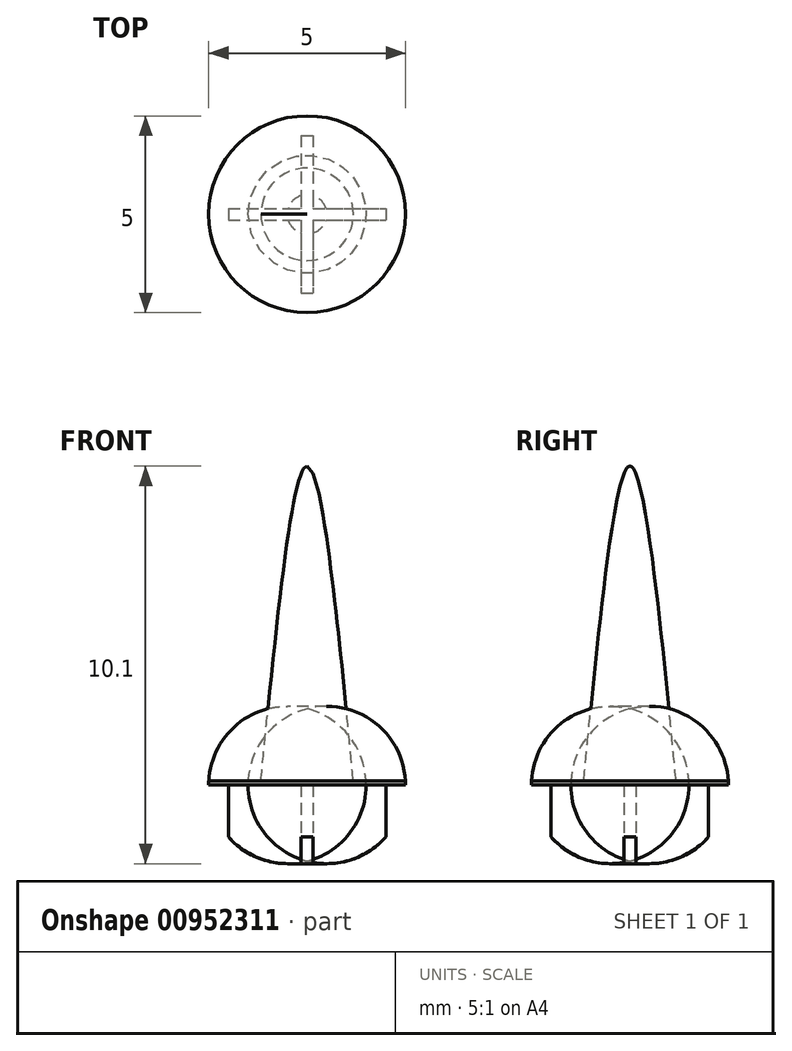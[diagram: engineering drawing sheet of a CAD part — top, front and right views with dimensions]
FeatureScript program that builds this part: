
annotation { "Feature Type Name" : "Feature", "Feature Type Description" : "" }
export const myFeature = defineFeature(function(context is Context, id is Id, definition is map)
    precondition{}
    {
        {
            var Q0;
            Q0=qCreatedBy(makeId("Top.planeOp"),FACE);
            var sketch = newSketch(context, id + "F0", { "sketchPlane" : qUnion([Q0])});
            skCircle(sketch, "E0", {"center": v(0, 0) * mm, "radius": 2.5 * mm});
            skSolve(sketch);
        }
        {
            var Q0;
            Q0=qSketchRegion(id+"F0",true);
            extrude(context, id + "F1", {"entities" : qUnion([Q0]), "depth" : 2.1 * mm, "offsetDistance" : 25 * mm});
        }
        {
            var Q0;
            Q0=makeQuery(id+"F1.opExtrude","CAP_FACE",FACE,{"disambiguationData":[OSD([sQuery(id+"F0.wireOp",EDGE,"E0")])],"isStart":false});
            var sketch = newSketch(context, id + "F2", { "sketchPlane" : qUnion([Q0])});
            skCircle(sketch, "E1", {"center": v(0, 0) * mm, "radius": 1.18 * mm});
            skSolve(sketch);
        }
        {
            var Q0;
            Q0=makeQuery(id+"F2.imprint","IMPRINT",FACE,{"disambiguationData":[TD([[makeQuery(id+"F2.imprint","IMPRINT",EDGE,{"derivedFrom":sQuery(id+"F2.wireOp",EDGE,"E1")}),-1.0]])]});
            cPlane(context, id + "F3", {"entities" : qUnion([Q0]), "cplaneType" : CPlaneType.OFFSET, "offset" : 8 * mm, "width" : 150 * mm, "height" : 150 * mm});
        }
        {
            var Q0;
            Q0=qCreatedBy(id+"F3.planeOp",FACE);
            var sketch = newSketch(context, id + "F4", { "sketchPlane" : qUnion([Q0])});
            skCircle(sketch, "E2", {"center": v(0, 0) * mm, "radius": 0.1 * mm});
            skSolve(sketch);
        }
        {
            var Q0;
            Q0=makeQuery(id+"F2.imprint","IMPRINT",FACE,{"disambiguationData":[TD([[makeQuery(id+"F2.imprint","IMPRINT",EDGE,{"derivedFrom":sQuery(id+"F2.wireOp",EDGE,"E1")}),1.0]])]});
            var Q1;
            Q1=sQuery(id+"F4.wireOp",VERTEX,"E2.center");
            loft(context, id + "F5", {"operationType" : NewBodyOperationType.ADD, "sheetProfilesArray" : [{ "sheetProfileEntities" : qUnion([Q0]) }, { "sheetProfileEntities" : qUnion([Q1]) }], "endCondition" : LoftEndDerivativeType.TANGENT_TO_PROFILE, "endMagnitude" : 1});
        }
        {
            var Q0;
            Q0=makeQuery(id+"F1.opExtrude","CAP_FACE",FACE,{"disambiguationData":[OSD([sQuery(id+"F0.wireOp",EDGE,"E0")])],"isStart":true});
            var sketch = newSketch(context, id + "F6", { "sketchPlane" : qUnion([Q0])});
            skSolve(sketch);
        }
        {
            var Q0;
            Q0=makeQuery(id+"F1.opExtrude","CAP_FACE",FACE,{"disambiguationData":[OSD([sQuery(id+"F0.wireOp",EDGE,"E0")])],"isStart":true});
            fillet(context, id + "F7", {"entities" : qUnion([Q0]), "radius" : 2 * mm, "tangentPropagation" : true, "defaultsChanged" : true, "vertexSettings" : [], "allowEdgeOverflow" : false});
        }
        {
            var Q0;
            Q0=makeQuery(id+"F6.imprint","IMPRINT",FACE,{"disambiguationData":[TD([[makeQuery(id+"F6.imprint","IMPRINT",EDGE,{"derivedFrom":makeQuery(id+"F1.opExtrude","CAP_EDGE",EDGE,{"disambiguationData":[OSD([sQuery(id+"F0.wireOp",EDGE,"E0")])],"isStart":true})}),-1.0]])]});
            var sketch = newSketch(context, id + "F8", { "sketchPlane" : qUnion([Q0])});
            skLineSegment(sketch, "E3.bottom", {"start": v(-0.15, -2) * mm, "end": v(0.15, -2) * mm});
            skLineSegment(sketch, "E3.top", {"start": v(-0.15, 2) * mm, "end": v(0.15, 2) * mm});
            skLineSegment(sketch, "E3.left", {"start": v(-0.15, -2) * mm, "end": v(-0.15, -0.15) * mm});
            skLineSegment(sketch, "E3.right", {"start": v(0.15, -2) * mm, "end": v(0.15, -0.15) * mm});
            skPoint(sketch, "E3.middle", {"position": v(0, 0) * mm});
            skLineSegment(sketch, "E4.bottom", {"start": v(-2, -0.15) * mm, "end": v(-0.15, -0.15) * mm});
            skLineSegment(sketch, "E4.top", {"start": v(-2, 0.15) * mm, "end": v(-0.15, 0.15) * mm});
            skLineSegment(sketch, "E4.left", {"start": v(-2, -0.15) * mm, "end": v(-2, 0.15) * mm});
            skLineSegment(sketch, "E4.right", {"start": v(2, -0.15) * mm, "end": v(2, 0.15) * mm});
            skLineSegment(sketch, "E5.trimOffspring", {"start": v(-0.15, 0.15) * mm, "end": v(-0.15, 2) * mm});
            skLineSegment(sketch, "E6.trimOffspring", {"start": v(0.15, 0.15) * mm, "end": v(2, 0.15) * mm});
            skLineSegment(sketch, "E7.trimOffspring", {"start": v(0.15, -0.15) * mm, "end": v(2, -0.15) * mm});
            skLineSegment(sketch, "E8.trimOffspring", {"start": v(0.15, 0.15) * mm, "end": v(0.15, 2) * mm});
            skSolve(sketch);
        }
        {
            var Q0;
            {var subQ0=sQuery(id+"F8.wireOp",EDGE,"E3.top");Q0=makeQuery(id+"F8.imprint","IMPRINT",FACE,{"disambiguationData":[TD([[makeQuery(id+"F8.imprint","IMPRINT",EDGE,{"derivedFrom":subQ0}),-1.0]])]});}
            var Q1;
            {var subQ0=sQuery(id+"F8.wireOp",EDGE,"E3.bottom");Q1=makeQuery(id+"F8.imprint","IMPRINT",FACE,{"disambiguationData":[TD([[makeQuery(id+"F8.imprint","IMPRINT",EDGE,{"derivedFrom":subQ0}),1.0]])]});}
            var Q2;
            {var subQ5=sQuery(id+"F8.wireOp",EDGE,"E4.left");Q2=makeQuery(id+"F8.imprint","IMPRINT",FACE,{"disambiguationData":[TD([[makeQuery(id+"F8.imprint","IMPRINT",EDGE,{"derivedFrom":subQ5}),-1.0]])]});}
            var Q3;
            {var subQ5=sQuery(id+"F8.wireOp",EDGE,"E4.right");Q3=makeQuery(id+"F8.imprint","IMPRINT",FACE,{"disambiguationData":[TD([[makeQuery(id+"F8.imprint","IMPRINT",EDGE,{"derivedFrom":subQ5}),1.0]])]});}
            extrude(context, id + "F9", {"entities" : qUnion([Q0, Q1, Q2, Q3]), "operationType" : NewBodyOperationType.REMOVE, "oppositeDirection" : true, "depth" : 2 * mm, "offsetDistance" : 25 * mm});
        }
    });
